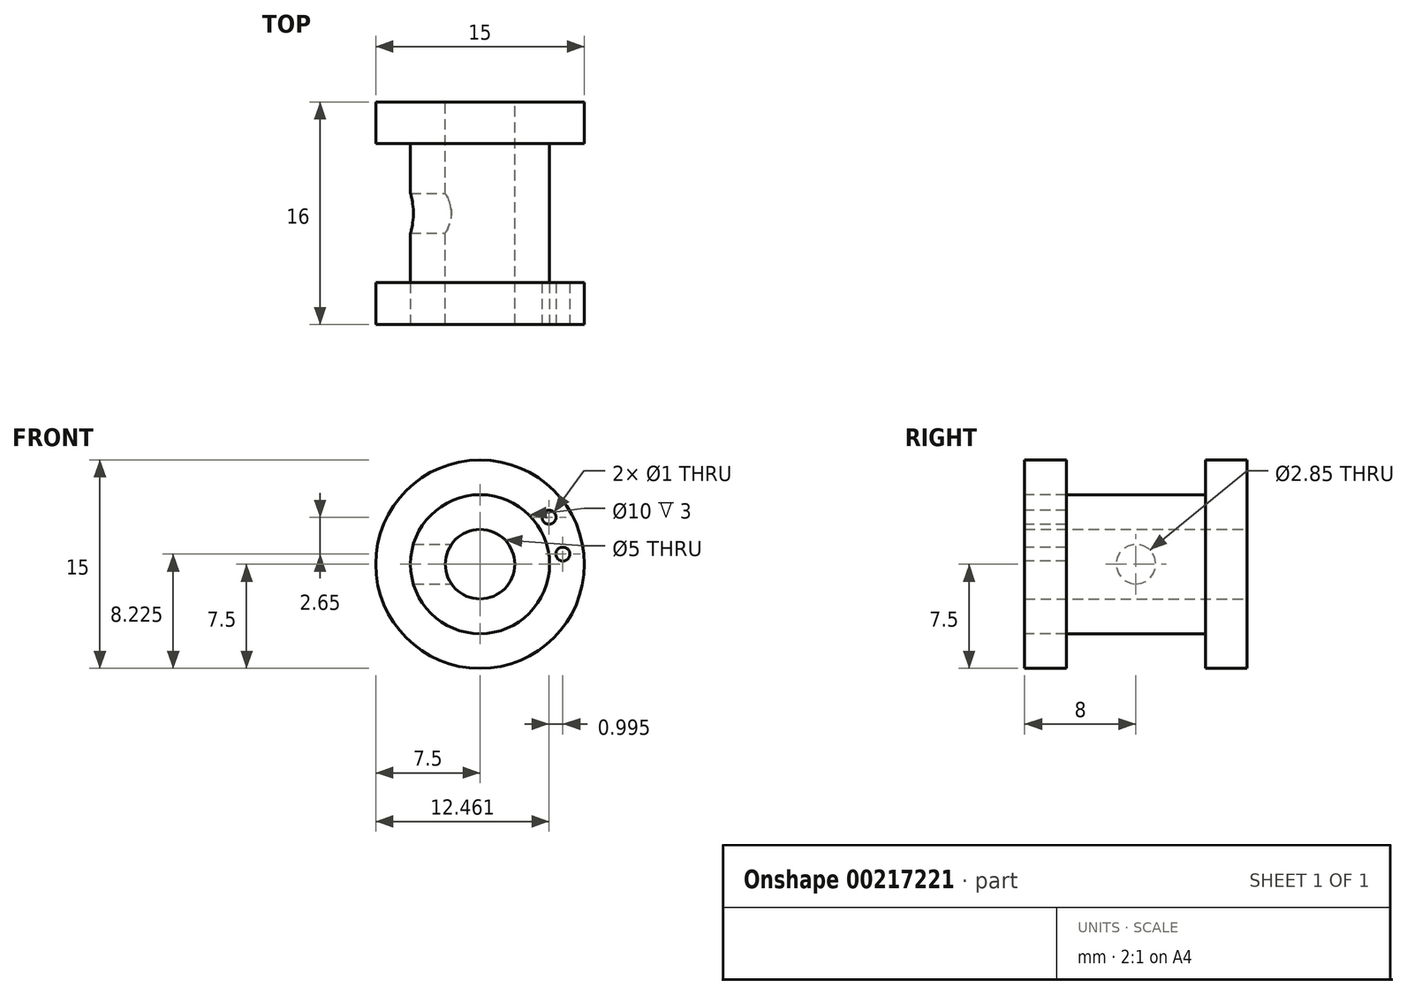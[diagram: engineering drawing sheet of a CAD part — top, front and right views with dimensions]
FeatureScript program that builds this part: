
annotation { "Feature Type Name" : "Feature", "Feature Type Description" : "" }
export const myFeature = defineFeature(function(context is Context, id is Id, definition is map)
    precondition{}
    {
        {
            var Q0;
            Q0=qCreatedBy(makeId("Front.planeOp"),FACE);
            var sketch = newSketch(context, id + "F0", { "sketchPlane" : qUnion([Q0])});
            skCircle(sketch, "E0", {"center": v(0, 0) * mm, "radius": 2.5 * mm});
            skCircle(sketch, "E1", {"center": v(0, 0) * mm, "radius": 5 * mm});
            skCircle(sketch, "E2", {"center": v(0, 0) * mm, "radius": 7.5 * mm});
            skSolve(sketch);
        }
        {
            var Q0;
            Q0=makeQuery(id+"F0.imprint","IMPRINT",FACE,{"disambiguationData":[TD([[makeQuery(id+"F0.imprint","IMPRINT",EDGE,{"derivedFrom":sQuery(id+"F0.wireOp",EDGE,"E0")}),-1.0]])]});
            extrude(context, id + "F1", {"entities" : qUnion([Q0]), "depth" : 13 * mm});
        }
        {
            var Q0;
            Q0=makeQuery(id+"F0.imprint","IMPRINT",FACE,{"disambiguationData":[TD([[makeQuery(id+"F0.imprint","IMPRINT",EDGE,{"derivedFrom":sQuery(id+"F0.wireOp",EDGE,"E1")}),-1.0]])]});
            extrude(context, id + "F2", {"entities" : qUnion([Q0]), "oppositeDirection" : true, "depth" : (3) * mm});
        }
        {
            var Q0;
            Q0=makeQuery(id+"F1.opExtrude","CAP_FACE",FACE,{"disambiguationData":[OSD([sQuery(id+"F0.wireOp",EDGE,"E0"),sQuery(id+"F0.wireOp",EDGE,"E1")])],"isStart":false});
            var sketch = newSketch(context, id + "F3", { "sketchPlane" : qUnion([Q0])});
            skCircle(sketch, "E3", {"center": v(0, 0) * mm, "radius": 7.5 * mm});
            skCircle(sketch, "E4", {"center": v(4.96, 3.37) * mm, "radius": 0.5 * mm});
            skCircle(sketch, "E5", {"center": v(5.96, 0.72) * mm, "radius": 0.5 * mm});
            skCircle(sketch, "E6", {"center": v(0, 0) * mm, "radius": 6 * mm, "construction": true});
            skSolve(sketch);
        }
        {
            var Q0;
            Q0=makeQuery(id+"F1.opExtrude","CAP_FACE",FACE,{"disambiguationData":[OSD([sQuery(id+"F0.wireOp",EDGE,"E0"),sQuery(id+"F0.wireOp",EDGE,"E1")])],"isStart":true});
            extrude(context, id + "F4", {"entities" : qUnion([Q0]), "operationType" : NewBodyOperationType.ADD, "depth" : 3 * mm});
        }
        {
            var Q0;
            Q0=makeQuery(id+"F3.imprint","IMPRINT",FACE,{"disambiguationData":[TD([[makeQuery(id+"F3.imprint","IMPRINT",EDGE,{"derivedFrom":sQuery(id+"F3.wireOp",EDGE,"E3")}),1.0]])]});
            extrude(context, id + "F5", {"entities" : qUnion([Q0]), "oppositeDirection" : true, "depth" : 3 * mm});
        }
        {
            var Q0;
            Q0=qCreatedBy(makeId("Right.planeOp"),FACE);
            var sketch = newSketch(context, id + "F6", { "sketchPlane" : qUnion([Q0])});
            skCircle(sketch, "E7", {"center": v(-5, 0) * mm, "radius": 1.43 * mm});
            skLineSegment(sketch, "E8", {"start": v(0, 0) * mm, "end": v(-10, 0) * mm, "construction": true});
            skSolve(sketch);
        }
        {
            var Q0;
            Q0 = qSketchRegion(id + "F6", true);
            extrude(context, id + "F7", {"entities" : qUnion([Q0]), "operationType" : NewBodyOperationType.REMOVE, "oppositeDirection" : true, "depth" : 25 * mm});
        }
    });
